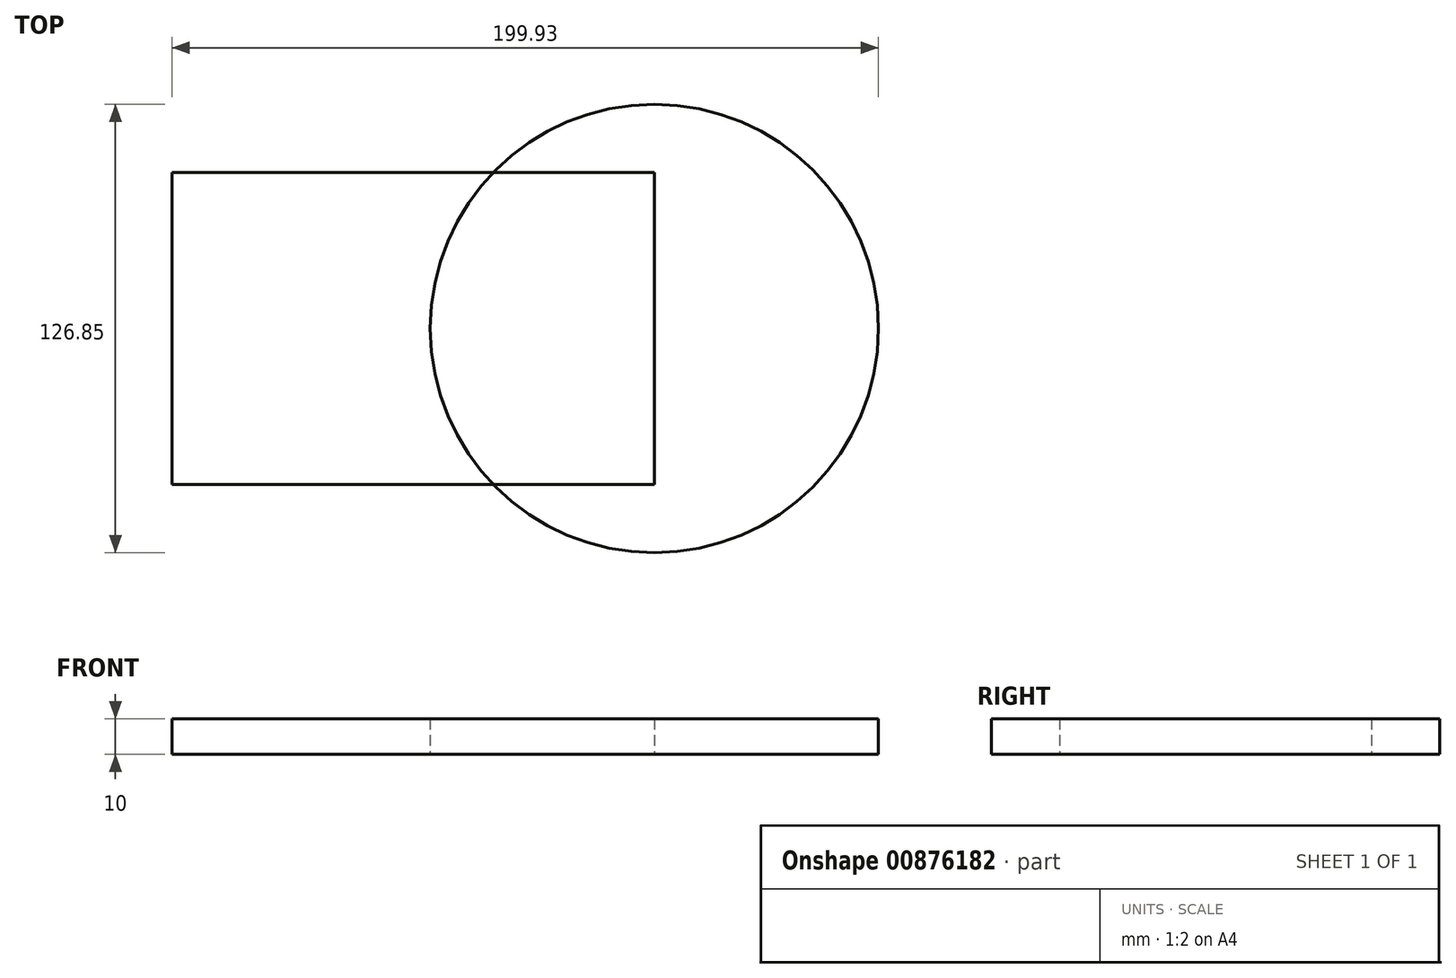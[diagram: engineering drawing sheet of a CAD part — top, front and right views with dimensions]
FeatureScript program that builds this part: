
annotation { "Feature Type Name" : "Feature", "Feature Type Description" : "" }
export const myFeature = defineFeature(function(context is Context, id is Id, definition is map)
    precondition{}
    {
        {
            var Q0;
            Q0=qCreatedBy(makeId("Top.planeOp"),FACE);
            var sketch = newSketch(context, id + "F0", { "sketchPlane" : qUnion([Q0])});
            skLineSegment(sketch, "E0.bottom", {"start": v(-136.5, 17.32) * mm, "end": v(0, 17.32) * mm});
            skLineSegment(sketch, "E0.top", {"start": v(-136.5, -70.89) * mm, "end": v(0, -70.89) * mm});
            skLineSegment(sketch, "E0.left", {"start": v(-136.5, 17.32) * mm, "end": v(-136.5, -70.89) * mm});
            skLineSegment(sketch, "E0.right", {"start": v(0, 17.32) * mm, "end": v(0, -70.89) * mm});
            skSolve(sketch);
        }
        {
            var Q0;
            Q0=qCreatedBy(makeId("Top.planeOp"),FACE);
            var sketch = newSketch(context, id + "F1", { "sketchPlane" : qUnion([Q0])});
            skCircle(sketch, "E1", {"center": v(0, -26.78) * mm, "radius": 63.42 * mm});
            skSolve(sketch);
        }
        {
            var Q0;
            Q0=makeQuery(id+"F0.imprint","IMPRINT",FACE,{"disambiguationData":[TD([[makeQuery(id+"F0.imprint","IMPRINT",EDGE,{"derivedFrom":sQuery(id+"F0.wireOp",EDGE,"E0.bottom")}),-1.0]])]});
            var Q1;
            Q1=makeQuery(id+"F1.imprint","IMPRINT",FACE,{"disambiguationData":[TD([[makeQuery(id+"F1.imprint","IMPRINT",EDGE,{"derivedFrom":sQuery(id+"F1.wireOp",EDGE,"E1")}),1.0]])]});
            extrude(context, id + "F2", {"entities" : qUnion([Q0, Q1]), "depth" : 10 * mm, "offsetDistance" : 25.4 * mm});
        }
    });
